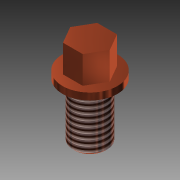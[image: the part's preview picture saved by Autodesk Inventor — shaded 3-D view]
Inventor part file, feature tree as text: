
AUTODESK INVENTOR PART (.ipt)
format: ipt  version: 2015 (Build 190159000, 159)  size: 104,960 bytes
history: native  units: mm
features: extrude x3, sketch x3, thread x1, chamfer x1
ambient origin geometry x8: Origin, YZ Plane, XZ Plane, XY Plane, X Axis, Y Axis, Z Axis, Center Point
bodies: 实体1 (feature_tree)
feature tree (8):
  extrude  "拉伸1"  Depth=1.0mm TaperAngle=0.0deg
  extrude  "拉伸2"  Depth=4.0mm TaperAngle=0.0deg
  extrude  "拉伸3"  Depth=8.0mm TaperAngle=0.0deg
  thread  "螺纹1"  [1 undecoded]
  chamfer  "倒角1"  Distance=0.25mm Angle=45.0deg
  sketch  "草图1"  dims[d0=8.0mm d1=1.0mm d2=0.0mm]
  sketch  "草图2"  dims[d3=5.0mm d4=4.0mm d5=0.0mm]
  sketch  "草图3"  dims[d6=5.0mm d7=8.0mm d8=0.0mm d9=10.0mm d10=0.0mm d11=0.25mm d12=2.0mm d13=45.0deg]
note: 1 required parameter value undecoded (feature->parameter linkage not recoverable at this tier; creation-order binding heuristic only, values carry confidence <= 0.55)
